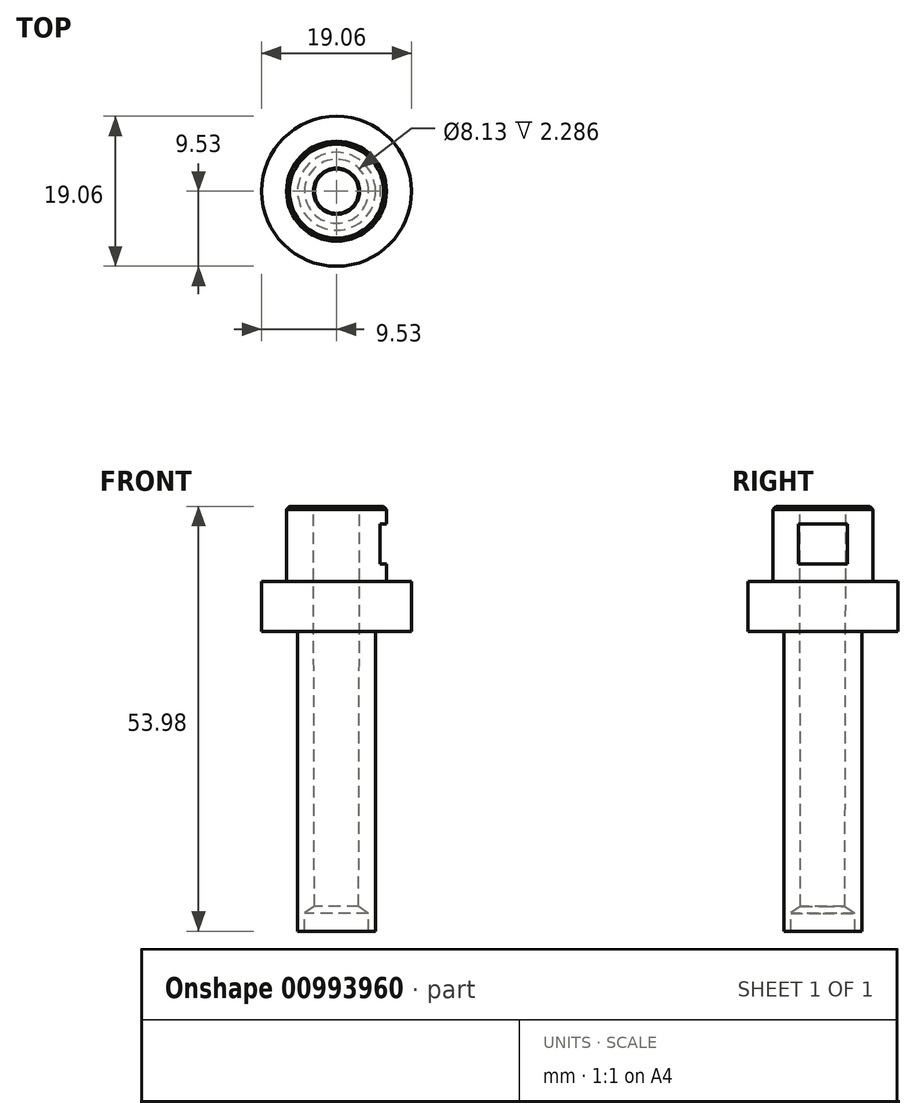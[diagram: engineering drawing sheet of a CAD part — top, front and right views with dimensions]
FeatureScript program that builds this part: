
annotation { "Feature Type Name" : "Feature", "Feature Type Description" : "" }
export const myFeature = defineFeature(function(context is Context, id is Id, definition is map)
    precondition{}
    {
        {
            var Q0;
            Q0=qCreatedBy(makeId("Front.planeOp"),FACE);
            var sketch = newSketch(context, id + "F0", { "sketchPlane" : qUnion([Q0])});
            skLineSegment(sketch, "E0", {"start": v(0, 0) * mm, "end": v(0, 53.98) * mm});
            skLineSegment(sketch, "E1", {"start": v(9.52, 44.45) * mm, "end": v(9.52, 38.1) * mm});
            skLineSegment(sketch, "E2", {"start": v(9.52, 38.1) * mm, "end": v(4.95, 38.1) * mm});
            skLineSegment(sketch, "E3", {"start": v(4.95, 38.1) * mm, "end": v(4.95, 0) * mm});
            skLineSegment(sketch, "E4", {"start": v(4.95, 0) * mm, "end": v(0, 0) * mm});
            skLineSegment(sketch, "E5", {"start": v(0, 53.98) * mm, "end": v(6.35, 53.98) * mm});
            skLineSegment(sketch, "E6", {"start": v(6.35, 53.98) * mm, "end": v(6.35, 44.45) * mm});
            skLineSegment(sketch, "E7", {"start": v(6.35, 44.45) * mm, "end": v(9.52, 44.45) * mm});
            skSolve(sketch);
        }
        {
            var Q0;
            Q0=makeQuery(id+"F0.imprint","IMPRINT",FACE,{"disambiguationData":[TD([[makeQuery(id+"F0.imprint","IMPRINT",EDGE,{"derivedFrom":sQuery(id+"F0.wireOp",EDGE,"E0")}),-1.0]])]});
            var Q1;
            Q1=sQuery(id+"F0.wireOp",EDGE,"E0");
            revolve(context, id + "F1", {"surfaceOperationType" : NewSurfaceOperationType.NEW, "entities" : qUnion([Q0]), "axis" : qUnion([Q1]), "revolveType" : RevolveType.FULL});
        }
        {
            var Q0;
            Q0=qCreatedBy(makeId("Front.planeOp"),FACE);
            var sketch = newSketch(context, id + "F2", { "sketchPlane" : qUnion([Q0])});
            skLineSegment(sketch, "E8", {"start": v(4.06, -0.25) * mm, "end": v(4.06, 2.29) * mm});
            skLineSegment(sketch, "E9", {"start": v(4.06, 2.29) * mm, "end": v(2.81, 3.17) * mm});
            skLineSegment(sketch, "E10", {"start": v(4.06, -0.25) * mm, "end": v(0, -0.25) * mm});
            skLineSegment(sketch, "E11", {"start": v(0, -0.25) * mm, "end": v(0, 53.9) * mm});
            skLineSegment(sketch, "E12", {"start": v(2.94, 55.5) * mm, "end": v(2.81, 3.17) * mm});
            skLineSegment(sketch, "E13", {"start": v(2.94, 55.5) * mm, "end": v(0, 55.5) * mm});
            skLineSegment(sketch, "E14", {"start": v(0, 55.5) * mm, "end": v(0, 51.52) * mm});
            skSolve(sketch);
        }
        {
            var Q0;
            Q0 = qSketchRegion(id + "F2", true);
            var Q1;
            Q1=sQuery(id+"F2.wireOp",EDGE,"E11");
            revolve(context, id + "F3", {"operationType" : NewBodyOperationType.REMOVE, "surfaceOperationType" : NewSurfaceOperationType.NEW, "entities" : qUnion([Q0]), "axis" : qUnion([Q1]), "revolveType" : RevolveType.FULL, "oppositeDirection" : true});
        }
        {
            var Q0;
            Q0=makeQuery(id+"F1.opRevolve","SWEPT_EDGE",EDGE,{"disambiguationData":[OSD([sQuery(id+"F0.wireOp",EDGE,"E5"),sQuery(id+"F0.wireOp",EDGE,"E6")])]});
            chamfer(context, id + "F4", {"entities" : qUnion([Q0]), "width" : 0.38 * mm, "tangentPropagation" : true});
        }
        {
            var Q0;
            Q0=qCreatedBy(makeId("Front.planeOp"),FACE);
            var sketch = newSketch(context, id + "F5", { "sketchPlane" : qUnion([Q0])});
            skLineSegment(sketch, "E15.bottom", {"start": v(7.12, 51.75) * mm, "end": v(5.54, 51.75) * mm});
            skLineSegment(sketch, "E15.top", {"start": v(7.12, 46.67) * mm, "end": v(5.54, 46.67) * mm});
            skLineSegment(sketch, "E15.left", {"start": v(7.12, 51.75) * mm, "end": v(7.12, 46.67) * mm});
            skLineSegment(sketch, "E15.right", {"start": v(5.54, 51.75) * mm, "end": v(5.54, 46.67) * mm});
            skPoint(sketch, "E15.middle", {"position": v(6.33, 49.21) * mm});
            skSolve(sketch);
        }
        {
            var Q0;
            Q0=makeQuery(id+"F5.imprint","IMPRINT",FACE,{"disambiguationData":[TD([[makeQuery(id+"F5.imprint","IMPRINT",EDGE,{"derivedFrom":sQuery(id+"F5.wireOp",EDGE,"E15.bottom")}),1.0]])]});
            extrude(context, id + "F6", {"entities" : qUnion([Q0]), "operationType" : NewBodyOperationType.REMOVE, "endBound" : BoundingType.SYMMETRIC, "oppositeDirection" : true, "depth" : 25.4 * mm, "offsetDistance" : 25.4 * mm});
        }
    });
